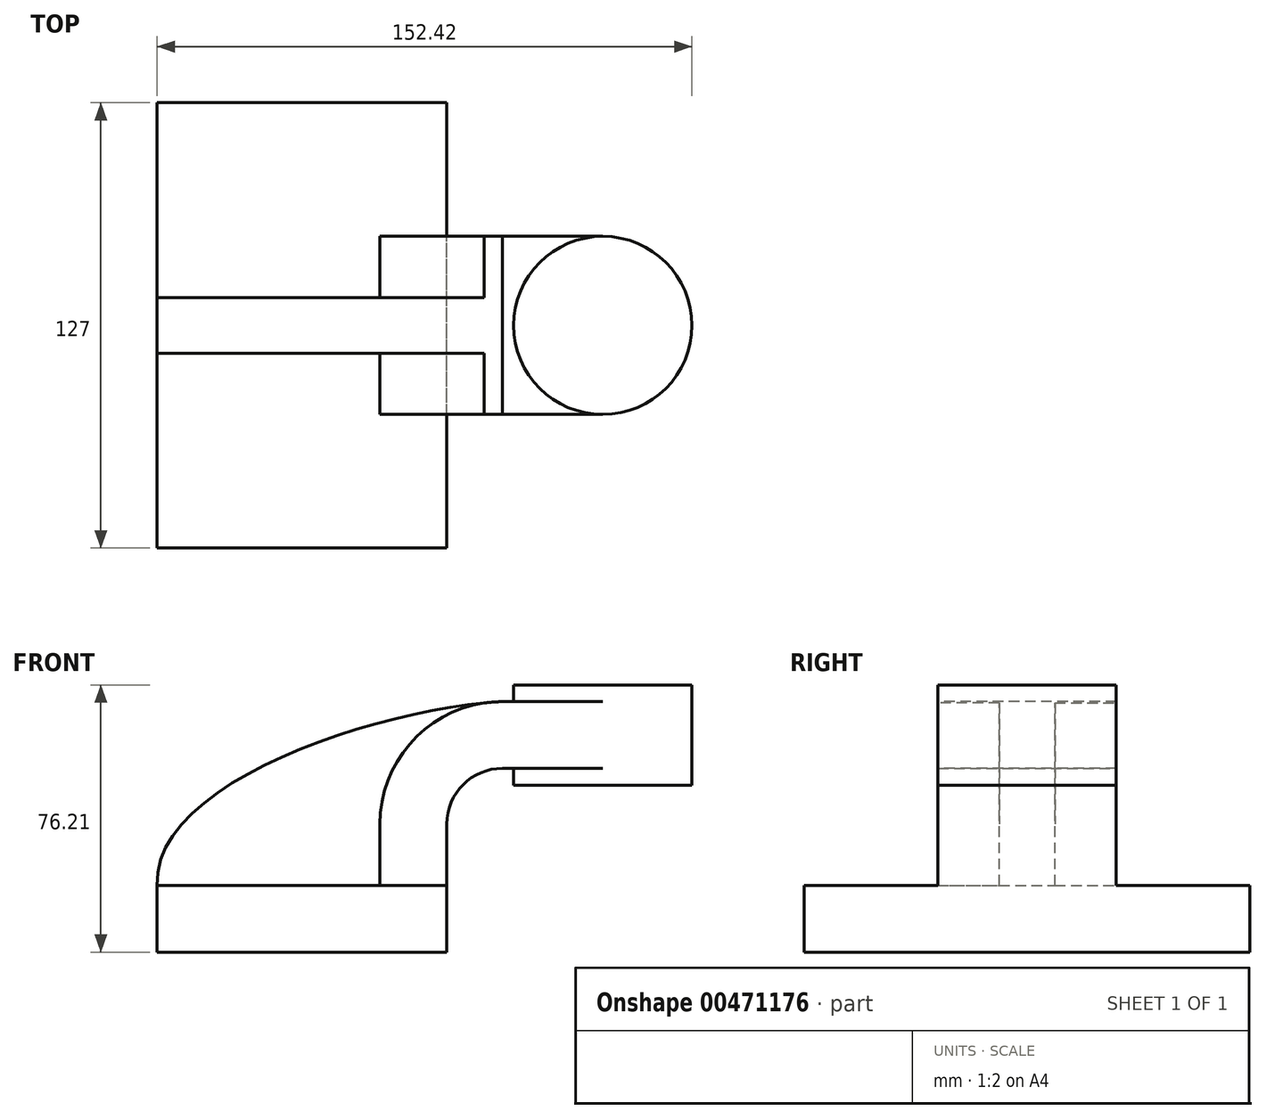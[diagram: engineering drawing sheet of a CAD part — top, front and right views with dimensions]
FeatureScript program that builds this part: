
annotation { "Feature Type Name" : "Feature", "Feature Type Description" : "" }
export const myFeature = defineFeature(function(context is Context, id is Id, definition is map)
    precondition{}
    {
        {
            var Q0;
            Q0=qCreatedBy(makeId("Front.planeOp"),FACE);
            var sketch = newSketch(context, id + "F0", { "sketchPlane" : qUnion([Q0])});
            skLineSegment(sketch, "E0.bottom", {"start": v(41.27, 9.53) * mm, "end": v(-41.28, 9.53) * mm});
            skLineSegment(sketch, "E0.top", {"start": v(41.28, -9.52) * mm, "end": v(-41.27, -9.52) * mm});
            skLineSegment(sketch, "E0.left", {"start": v(41.28, 9.53) * mm, "end": v(41.28, -9.52) * mm});
            skLineSegment(sketch, "E0.right", {"start": v(-41.28, 9.53) * mm, "end": v(-41.28, -9.52) * mm});
            skPoint(sketch, "E0.middle", {"position": v(0, 0) * mm});
            skLineSegment(sketch, "E1.bottom", {"start": v(60.32, 38.1) * mm, "end": v(111.12, 38.1) * mm});
            skLineSegment(sketch, "E1.top", {"start": v(60.32, 66.68) * mm, "end": v(111.12, 66.68) * mm});
            skLineSegment(sketch, "E1.left", {"start": v(60.32, 38.1) * mm, "end": v(60.32, 66.68) * mm});
            skLineSegment(sketch, "E1.right", {"start": v(111.12, 38.1) * mm, "end": v(111.12, 66.68) * mm});
            skPoint(sketch, "E1.middle", {"position": v(85.72, 52.39) * mm});
            skLineSegment(sketch, "E2", {"start": v(41.27, 9.53) * mm, "end": v(41.27, 27) * mm});
            skArc(sketch, "E3", {"start": v(41.27, 27) * mm, "mid": v(45.92, 38.23) * mm, "end": v(57.15, 42.88) * mm});
            skLineSegment(sketch, "E4", {"start": v(57.15, 42.88) * mm, "end": v(85.72, 42.88) * mm});
            skLineSegment(sketch, "E5.0", {"start": v(57.15, 61.93) * mm, "end": v(85.72, 61.93) * mm});
            skArc(sketch, "E5.1", {"start": v(22.22, 27) * mm, "mid": v(32.45, 51.7) * mm, "end": v(57.15, 61.93) * mm});
            skLineSegment(sketch, "E5.2", {"start": v(22.22, 9.53) * mm, "end": v(22.22, 27) * mm});
            skFitSpline(sketch, "E6", {"points": [v(-41.28, 9.53) * mm, v(57.15, 61.93) * mm], "startDerivative": vector(-3.82, 90.17) * mm, "endDerivative": vector(101.12, 5.24) * mm});
            skLineSegment(sketch, "E7", {"start": v(85.72, 66.68) * mm, "end": v(85.72, 38.1) * mm});
            skSolve(sketch);
        }
        {
            var Q0;
            Q0=makeQuery(id+"F0.imprint","IMPRINT",FACE,{"disambiguationData":[TD([[makeQuery(id+"F0.imprint","IMPRINT",EDGE,{"derivedFrom":sQuery(id+"F0.wireOp",EDGE,"E0.top")}),-1.0]])]});
            extrude(context, id + "F1", {"entities" : qUnion([Q0]), "endBound" : BoundingType.SYMMETRIC, "depth" : 127 * mm});
        }
        {
            var Q0;
            {var subQ3=sQuery(id+"F0.wireOp",EDGE,"E5.2");Q0=makeQuery(id+"F0.imprint","IMPRINT",FACE,{"disambiguationData":[TD([[makeQuery(id+"F0.imprint","IMPRINT",EDGE,{"derivedFrom":subQ3}),1.0]])]});}
            extrude(context, id + "F2", {"entities" : qUnion([Q0]), "operationType" : NewBodyOperationType.ADD, "endBound" : BoundingType.SYMMETRIC, "depth" : 15.88 * mm});
        }
        {
            var Q0;
            {var subQ1=sQuery(id+"F0.wireOp",EDGE,"E2");Q0=makeQuery(id+"F0.imprint","IMPRINT",FACE,{"disambiguationData":[TD([[makeQuery(id+"F0.imprint","IMPRINT",EDGE,{"derivedFrom":subQ1}),1.0]])]});}
            var Q1;
            {var subQ0=sQuery(id+"F0.wireOp",EDGE,"E4");var subQ1=sQuery(id+"F0.wireOp",EDGE,"E1.left");var subQ2=makeQuery(id+"F0.imprint","INTERSECT",VERTEX,{"derivedFrom":[subQ1,subQ0]});Q1=makeQuery(id+"F0.imprint","IMPRINT",FACE,{"disambiguationData":[TD([[makeQuery(id+"F0.imprint","IMPRINT",EDGE,{"disambiguationData":[TD([[subQ2,-1.0]])],"derivedFrom":subQ1}),-1.0]])]});}
            extrude(context, id + "F3", {"entities" : qUnion([Q0, Q1]), "operationType" : NewBodyOperationType.ADD, "endBound" : BoundingType.SYMMETRIC, "depth" : 50.8 * mm});
        }
        {
            var Q0;
            {var subQ4=sQuery(id+"F0.wireOp",EDGE,"E1.right");Q0=makeQuery(id+"F0.imprint","IMPRINT",FACE,{"disambiguationData":[TD([[makeQuery(id+"F0.imprint","IMPRINT",EDGE,{"derivedFrom":subQ4}),1.0]])]});}
            var Q1;
            Q1=sQuery(id+"F0.wireOp",EDGE,"E7");
            revolve(context, id + "F4", {"operationType" : NewBodyOperationType.ADD, "entities" : qUnion([Q0]), "axis" : qUnion([Q1]), "revolveType" : RevolveType.FULL});
        }
    });
